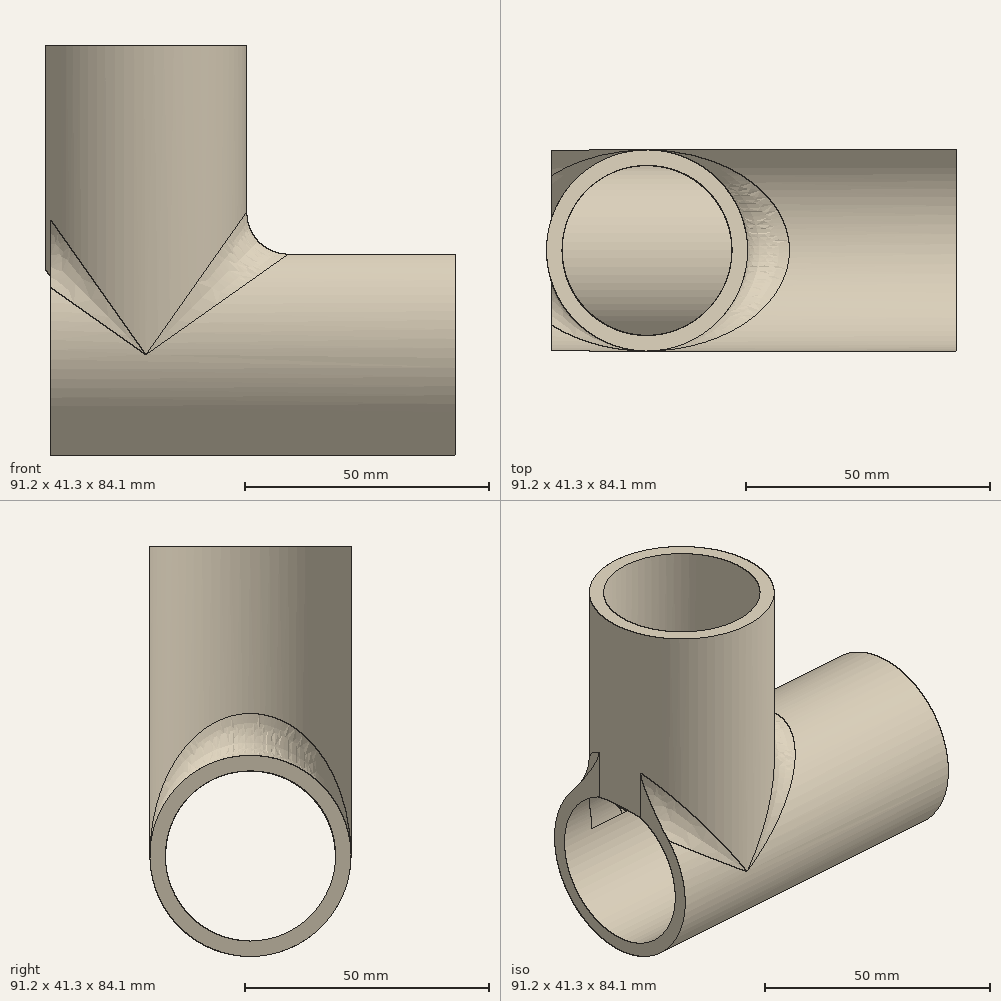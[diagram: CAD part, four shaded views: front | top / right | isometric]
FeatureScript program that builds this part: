
annotation { "Feature Type Name" : "Feature", "Feature Type Description" : "" }
export const myFeature = defineFeature(function(context is Context, id is Id, definition is map)
    precondition{}
    {
        {
            var Q0;
            Q0=qCreatedBy(makeId("Top.planeOp"),FACE);
            var sketch = newSketch(context, id + "F0", { "sketchPlane" : qUnion([Q0])});
            skCircle(sketch, "E0", {"center": v(0, 0) * mm, "radius": 17.46 * mm});
            skCircle(sketch, "E1", {"center": v(0, 0) * mm, "radius": 20.64 * mm});
            skSolve(sketch);
        }
        {
            var Q0;
            Q0=makeQuery(id+"F0.imprint","IMPRINT",FACE,{"disambiguationData":[TD([[makeQuery(id+"F0.imprint","IMPRINT",EDGE,{"derivedFrom":sQuery(id+"F0.wireOp",EDGE,"E0")}),-1.0]])]});
            extrude(context, id + "F1", {"entities" : qUnion([Q0]), "depth" : 63.5 * mm, "offsetDistance" : 25.4 * mm});
        }
        {
            var Q0;
            Q0=qCreatedBy(makeId("Right.planeOp"),FACE);
            var sketch = newSketch(context, id + "F2", { "sketchPlane" : qUnion([Q0])});
            skCircle(sketch, "E2", {"center": v(0, 0) * mm, "radius": 20.64 * mm});
            skCircle(sketch, "E3", {"center": v(0, 0) * mm, "radius": 17.46 * mm});
            skSolve(sketch);
        }
        {
            var Q0;
            Q0=makeQuery(id+"F2.imprint","IMPRINT",FACE,{"disambiguationData":[TD([[makeQuery(id+"F2.imprint","IMPRINT",EDGE,{"derivedFrom":sQuery(id+"F2.wireOp",EDGE,"E2")}),1.0]])]});
            extrude(context, id + "F3", {"entities" : qUnion([Q0]), "operationType" : NewBodyOperationType.ADD, "depth" : 63.5 * mm, "offsetDistance" : 25.4 * mm, "hasSecondDirection" : true, "secondDirectionOppositeDirection" : true, "secondDirectionDepth" : 19.56 * mm});
        }
        {
            var Q0;
            Q0=qCreatedBy(makeId("Right.planeOp"),FACE);
            var sketch = newSketch(context, id + "F4", { "sketchPlane" : qUnion([Q0])});
            skCircle(sketch, "E4", {"center": v(0, 0) * mm, "radius": 17.4 * mm});
            skSolve(sketch);
        }
        {
            var Q0;
            Q0=makeQuery(id+"F4.imprint","IMPRINT",FACE,{"disambiguationData":[TD([[makeQuery(id+"F4.imprint","IMPRINT",EDGE,{"derivedFrom":sQuery(id+"F4.wireOp",EDGE,"E4")}),1.0]])]});
            extrude(context, id + "F5", {"entities" : qUnion([Q0]), "operationType" : NewBodyOperationType.REMOVE, "oppositeDirection" : true, "depth" : 25.4 * mm, "offsetDistance" : 25.4 * mm, "hasSecondDirection" : true, "secondDirectionOppositeDirection" : false, "secondDirectionDepth" : 80.77 * mm});
        }
        {
            var Q0;
            Q0=qCreatedBy(makeId("Top.planeOp"),FACE);
            var sketch = newSketch(context, id + "F6", { "sketchPlane" : qUnion([Q0])});
            skCircle(sketch, "E5", {"center": v(0, 0) * mm, "radius": 17.4 * mm});
            skSolve(sketch);
        }
        {
            var Q0;
            Q0=makeQuery(id+"F6.imprint","IMPRINT",FACE,{"disambiguationData":[TD([[makeQuery(id+"F6.imprint","IMPRINT",EDGE,{"derivedFrom":sQuery(id+"F6.wireOp",EDGE,"E5")}),1.0]])]});
            extrude(context, id + "F7", {"entities" : qUnion([Q0]), "operationType" : NewBodyOperationType.REMOVE, "depth" : 85.1 * mm, "offsetDistance" : 25.4 * mm});
        }
        {
            var Q0;
            Q0=makeQuery(id+"F3.boolean.opBoolean","INTERSECT",EDGE,{"disambiguationData":[OD(0.0)],"derivedFrom":[makeQuery(id+"F1.opExtrude","SWEPT_FACE",FACE,{"disambiguationData":[OSD([sQuery(id+"F0.wireOp",EDGE,"E1")])]}),makeQuery(id+"F3.opExtrude","SWEPT_FACE",FACE,{"disambiguationData":[OSD([sQuery(id+"F2.wireOp",EDGE,"E2")])]})]});
            fillet(context, id + "F8", {"entities" : qUnion([Q0]), "radius" : 8.58 * mm, "tangentPropagation" : true, "allowEdgeOverflow" : false});
        }
    });
